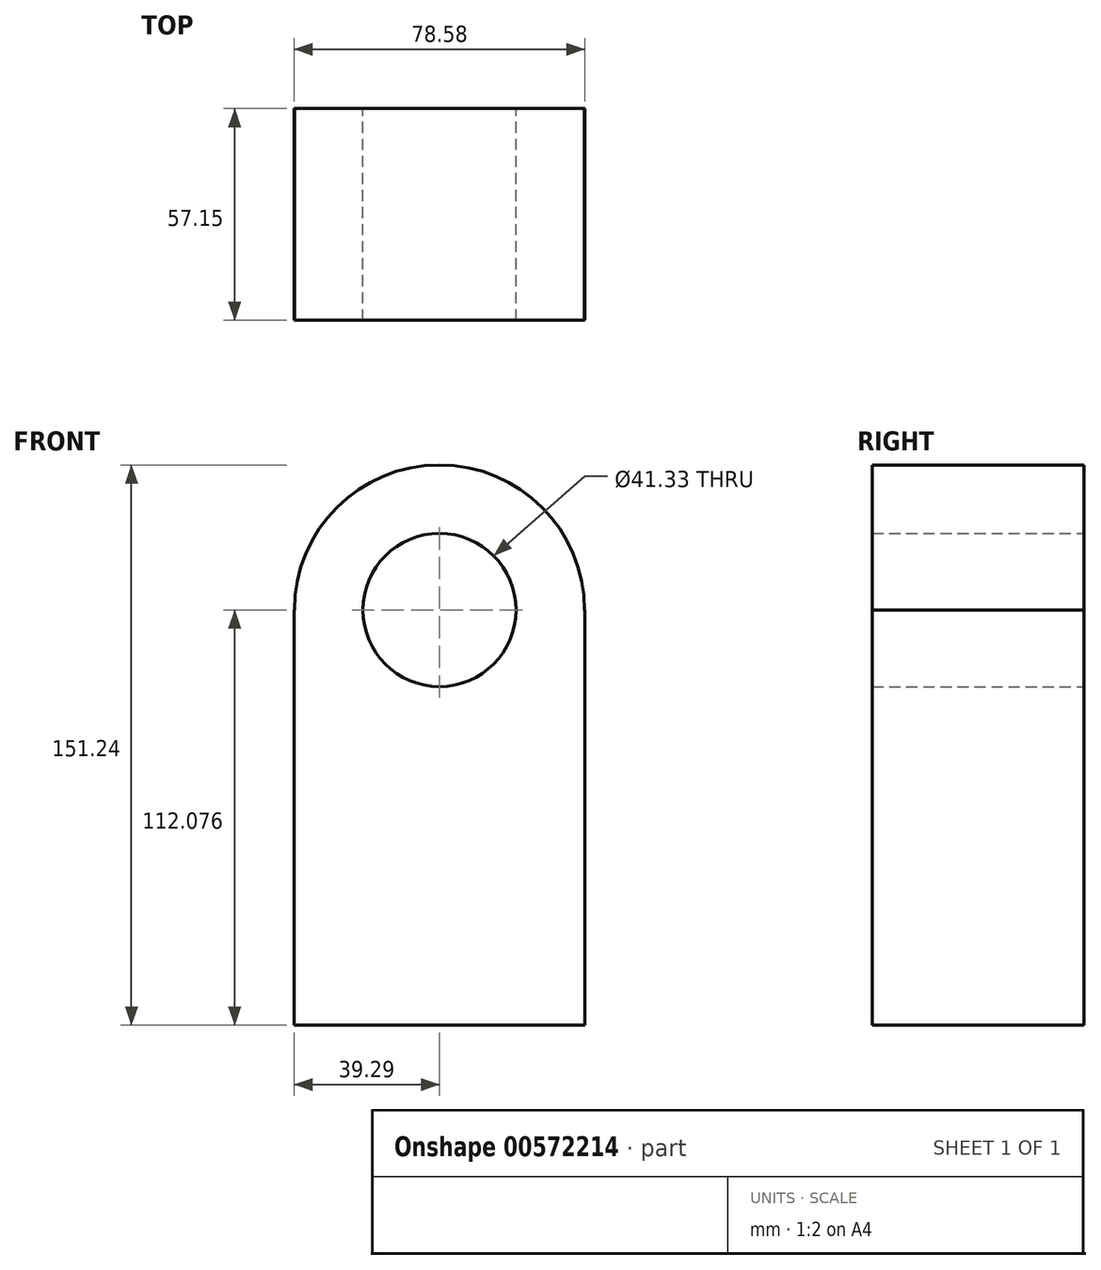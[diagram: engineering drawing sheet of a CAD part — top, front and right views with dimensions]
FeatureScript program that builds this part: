
annotation { "Feature Type Name" : "Feature", "Feature Type Description" : "" }
export const myFeature = defineFeature(function(context is Context, id is Id, definition is map)
    precondition{}
    {
        {
            var Q0;
            Q0=qCreatedBy(makeId("Front.planeOp"),FACE);
            var sketch = newSketch(context, id + "F0", { "sketchPlane" : qUnion([Q0])});
            skLineSegment(sketch, "E0.bottom", {"start": v(39.3, -56.04) * mm, "end": v(-39.3, -56.04) * mm});
            skLineSegment(sketch, "E0.top", {"start": v(39.3, 56.04) * mm, "end": v(39.16, 56.04) * mm});
            skLineSegment(sketch, "E0.left", {"start": v(39.3, -56.04) * mm, "end": v(39.3, 56.04) * mm});
            skLineSegment(sketch, "E0.right", {"start": v(-39.3, -56.04) * mm, "end": v(-39.3, 56.04) * mm});
            skPoint(sketch, "E0.middle", {"position": v(0, 0) * mm});
            skArc(sketch, "E1", {"start": v(39.16, 56.04) * mm, "mid": v(0, 95.2) * mm, "end": v(-39.16, 56.04) * mm});
            skCircle(sketch, "E2", {"center": v(0, 56.04) * mm, "radius": 20.67 * mm});
            skArc(sketch, "E3", {"start": v(-39.3, 56.04) * mm, "mid": v(0, 95.33) * mm, "end": v(39.3, 56.04) * mm});
            skLineSegment(sketch, "E4.trimOffspring", {"start": v(-39.16, 56.04) * mm, "end": v(-39.3, 56.04) * mm});
            skSolve(sketch);
        }
        {
            var Q0;
            Q0=makeQuery(id+"F0.imprint","IMPRINT",FACE,{"disambiguationData":[TD([[makeQuery(id+"F0.imprint","IMPRINT",EDGE,{"derivedFrom":sQuery(id+"F0.wireOp",EDGE,"E0.bottom")}),-1.0]])]});
            extrude(context, id + "F1", {"entities" : qUnion([Q0]), "depth" : 57.15 * mm, "offsetDistance" : 25.4 * mm});
        }
    });
